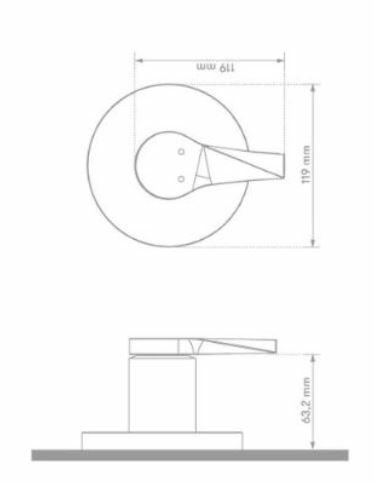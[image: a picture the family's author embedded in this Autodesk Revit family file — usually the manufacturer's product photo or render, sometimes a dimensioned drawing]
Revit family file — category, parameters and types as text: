
# Revit family: 01-1753-11-LLAVE MÓVIL PARED C CUERPO PLÁSTICO HELIX PALA
name_source: partatom
category: Plumbing Fixtures
revit_build: Autodesk Revit 2018 (Build: 20170223_1515(x64)
units: mm (PartAtom-declared; Revit-internal decimal feet)

## family parameters
Cut with Voids When Loaded = No
Host = Face
OmniClass Number = 23.31.11.00
Part Type = Normal
Room Calculation Point = No
Round Connector Dimension = Use Diameter
Shared = No

## types (1)
- 01-1753-11
    Alto = 298 mm  [stored 0.97769 ft]
    Ancho = 67 mm
    CW Connection = Yes
    Default Elevation = 0 mm  [stored 0 ft]
    Description = LLAVE MÓVIL PARED
    Finish = Plastico ABS Cromado
    HW Connection = Yes
    Largo = 260 mm
    Link Ficha Tecnica = http://infotecnica.gricol.com
    Manufacturer = Gricol
    Model = 01-1753-11
    Product Name = LLAVE MÓVIL PARED C CUERPO PLÁSTICO HELIX PALA
    Type Image = LLAVE MÓVIL PARED C CUERPO PLÁSTICO HELIX PALA PLANO.jpg
    URL = https://www.gricol.com
    Vent Connection = No
    Waste Connection = No

note: [stored X ft] marks values corroborated as IEEE doubles in the binary element streams (Revit-internal decimal feet)

## geometry (parser evidence)
native form markers: Blend x2, Sweep x7
no freeform markers — native parametric forms only
